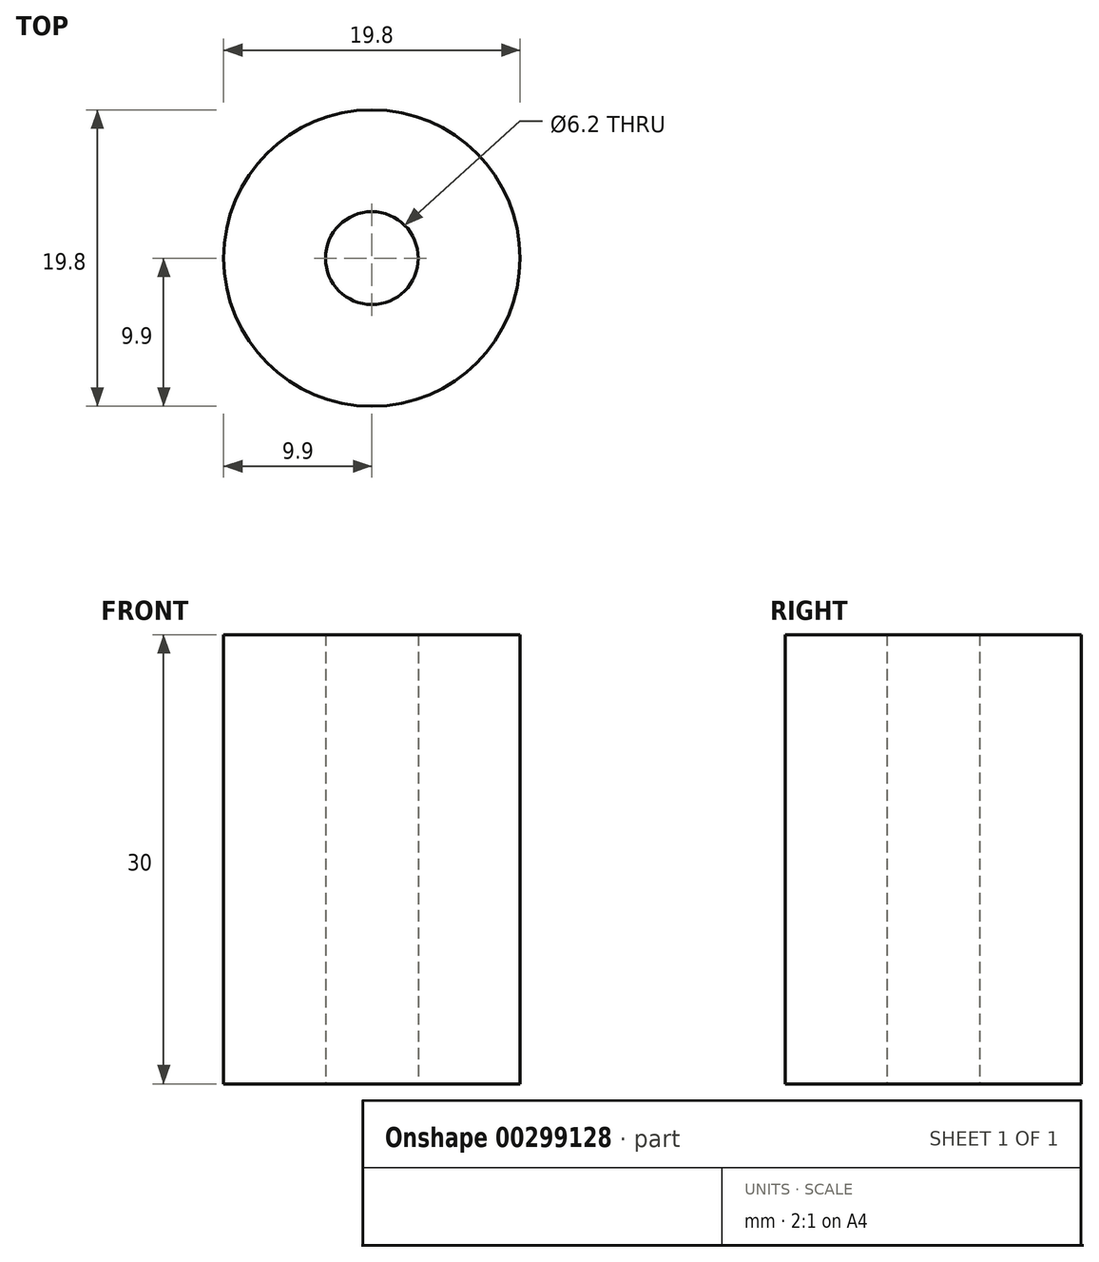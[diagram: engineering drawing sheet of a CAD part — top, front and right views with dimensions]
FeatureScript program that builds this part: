
annotation { "Feature Type Name" : "Feature", "Feature Type Description" : "" }
export const myFeature = defineFeature(function(context is Context, id is Id, definition is map)
    precondition{}
    {
        {
            var Q0;
            Q0=qCreatedBy(makeId("Top.planeOp"),FACE);
            var sketch = newSketch(context, id + "F0", { "sketchPlane" : qUnion([Q0])});
            skCircle(sketch, "E0", {"center": v(0, 0) * mm, "radius": 3.1 * mm});
            skCircle(sketch, "E1", {"center": v(0, 0) * mm, "radius": 9.9 * mm});
            skSolve(sketch);
        }
        {
            var Q0;
            Q0 = qSketchRegion(id + "F0", true);
            extrude(context, id + "F1", {"entities" : qUnion([Q0]), "depth" : 30 * mm});
        }
    });
